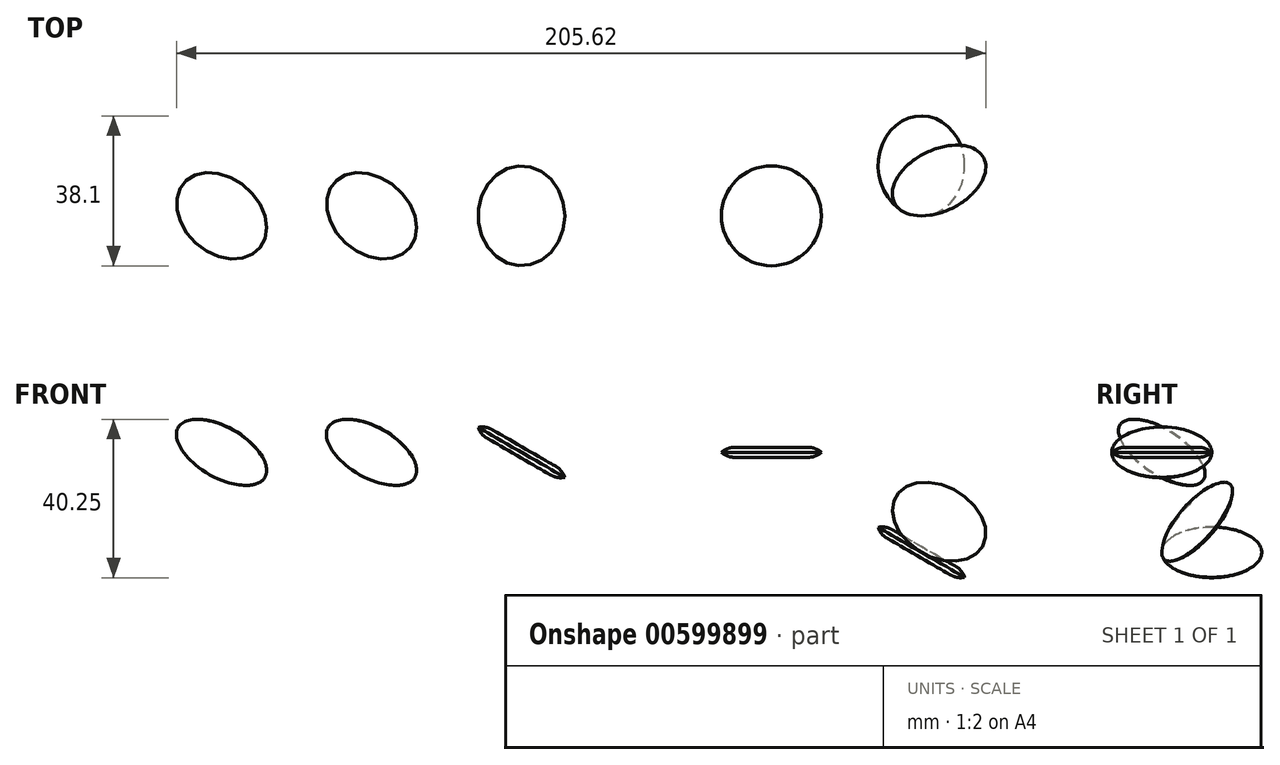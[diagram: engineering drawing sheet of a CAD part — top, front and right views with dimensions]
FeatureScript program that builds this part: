
annotation { "Feature Type Name" : "Feature", "Feature Type Description" : "" }
export const myFeature = defineFeature(function(context is Context, id is Id, definition is map)
    precondition{}
    {
        {
            var Q0;
            Q0=qCreatedBy(makeId("Top.planeOp"),FACE);
            var sketch = newSketch(context, id + "F0", { "sketchPlane" : qUnion([Q0])});
            skCircle(sketch, "E0", {"center": v(0, 0) * mm, "radius": 12.7 * mm});
            skSolve(sketch);
        }
        {
            var Q0;
            Q0 = qSketchRegion(id + "F0", true);
            extrude(context, id + "F1", {"entities" : qUnion([Q0]), "endBound" : BoundingType.SYMMETRIC, "depth" : 2.54 * mm, "offsetDistance" : 25.4 * mm});
        }
        {
            var Q0;
            Q0=makeQuery(id+"F1.opExtrude","CAP_EDGE",EDGE,{"disambiguationData":[OSD([sQuery(id+"F0.wireOp",EDGE,"E0")])],"isStart":true});
            var Q1;
            Q1=makeQuery(id+"F1.opExtrude","CAP_EDGE",EDGE,{"disambiguationData":[OSD([sQuery(id+"F0.wireOp",EDGE,"E0")])],"isStart":false});
            chamfer(context, id + "F2", {"entities" : qUnion([Q0, Q1]), "width" : 1.27 * mm, "tangentPropagation" : true});
        }
        {
            var Q0;
            {var subQ0=sQuery(id+"F0.wireOp",EDGE,"E0");Q0=makeQuery(id+"F2.opChamfer","BLEND_EDGE",EDGE,{"blendedFrom":[makeQuery(id+"F1.opExtrude","CAP_EDGE",EDGE,{"disambiguationData":[OSD([subQ0])],"isStart":false}),makeQuery(id+"F1.opExtrude","CAP_FACE",FACE,{"disambiguationData":[OSD([subQ0])],"isStart":false})],"blendedInto":[makeQuery(id+"F1.opExtrude","CAP_FACE",FACE,{"disambiguationData":[OSD([subQ0])],"isStart":false})]});}
            fillet(context, id + "F3", {"entities" : qUnion([Q0]), "radius" : 5.08 * mm, "tangentPropagation" : true, "allowEdgeOverflow" : false});
        }
        {
            var Q0;
            {var subQ0=sQuery(id+"F0.wireOp",EDGE,"E0");Q0=makeQuery(id+"F2.opChamfer","BLEND_EDGE",EDGE,{"blendedFrom":[makeQuery(id+"F1.opExtrude","CAP_EDGE",EDGE,{"disambiguationData":[OSD([subQ0])],"isStart":true}),makeQuery(id+"F1.opExtrude","CAP_FACE",FACE,{"disambiguationData":[OSD([subQ0])],"isStart":true})],"blendedInto":[makeQuery(id+"F1.opExtrude","CAP_FACE",FACE,{"disambiguationData":[OSD([subQ0])],"isStart":true})]});}
            fillet(context, id + "F4", {"entities" : qUnion([Q0]), "radius" : 5.08 * mm, "tangentPropagation" : true, "allowEdgeOverflow" : false});
        }
        {
            var Q0;
            Q0=makeQuery(id+"F1.opExtrude","SWEPT_BODY",BODY,{"disambiguationData":[OSD([sQuery(id+"F0.wireOp",EDGE,"E0")])]});
            transform(context, id + "F5", {"entities" : qUnion([Q0]), "transformType" : TransformType.TRANSLATION_3D, "dx" : 38.1 * mm, "dy" : 12.7 * mm, "dz" : -25.4 * mm, "makeCopy" : true});
        }
        {
            var Q0;
            Q0=makeQuery(id+"F5.opPattern","COPY",FACE,{"derivedFrom":makeQuery(id+"F1.opExtrude","CAP_FACE",FACE,{"disambiguationData":[OSD([sQuery(id+"F0.wireOp",EDGE,"E0")])],"isStart":false}),"instanceName":"1"});
            cPlane(context, id + "F6", {"entities" : qUnion([Q0]), "cplaneType" : CPlaneType.OFFSET, "offset" : 1.27 * mm, "oppositeDirection" : true, "width" : 152.4 * mm, "height" : 152.4 * mm});
        }
        {
            var Q0;
            Q0=qCreatedBy(id+"F6.planeOp",FACE);
            var sketch = newSketch(context, id + "F7", { "sketchPlane" : qUnion([Q0])});
            skCircle(sketch, "E1.0", {"center": v(38.1, 12.7) * mm, "radius": 9.34 * mm});
            skLineSegment(sketch, "E2", {"start": v(38.1, 12.7) * mm, "end": v(38.1, 37.81) * mm});
            skLineSegment(sketch, "E3", {"start": v(38.1, 37.81) * mm, "end": v(38.1, -2.87) * mm});
            skSolve(sketch);
        }
        {
            var Q0;
            Q0=makeQuery(id+"F5.opPattern","COPY",BODY,{"derivedFrom":makeQuery(id+"F1.opExtrude","SWEPT_BODY",BODY,{"disambiguationData":[OSD([sQuery(id+"F0.wireOp",EDGE,"E0")])]}),"instanceName":"1"});
            var Q1;
            Q1=sQuery(id+"F7.wireOp",EDGE,"E3");
            transform(context, id + "F8", {"entities" : qUnion([Q0]), "transformType" : TransformType.ROTATION, "transformAxis" : qUnion([Q1]), "angle" : 30 * degree, "oppositeDirection" : true, "makeCopy" : false});
        }
        {
            var Q0;
            Q0=makeQuery(id+"F5.opPattern","COPY",FACE,{"derivedFrom":makeQuery(id+"F1.opExtrude","CAP_FACE",FACE,{"disambiguationData":[OSD([sQuery(id+"F0.wireOp",EDGE,"E0")])],"isStart":false}),"instanceName":"1"});
            cPlane(context, id + "F9", {"entities" : qUnion([Q0]), "cplaneType" : CPlaneType.OFFSET, "offset" : 1.27 * mm, "oppositeDirection" : true, "width" : 152.4 * mm, "height" : 152.4 * mm});
        }
        {
            var Q0;
            Q0=qCreatedBy(id+"F9.planeOp",FACE);
            var sketch = newSketch(context, id + "F10", { "sketchPlane" : qUnion([Q0])});
            skCircle(sketch, "E4.0", {"center": v(45.7, 12.7) * mm, "radius": 12.7 * mm});
            skLineSegment(sketch, "E5", {"start": v(45.7, 0) * mm, "end": v(60.1, 0) * mm});
            skLineSegment(sketch, "E6", {"start": v(60.1, 0) * mm, "end": v(20.4, 0) * mm});
            skSolve(sketch);
        }
        {
            var Q0;
            Q0=makeQuery(id+"F5.opPattern","COPY",BODY,{"derivedFrom":makeQuery(id+"F1.opExtrude","SWEPT_BODY",BODY,{"disambiguationData":[OSD([sQuery(id+"F0.wireOp",EDGE,"E0")])]}),"instanceName":"1"});
            var Q1;
            Q1=sQuery(id+"F10.wireOp",EDGE,"E6");
            transform(context, id + "F11", {"entities" : qUnion([Q0]), "transformType" : TransformType.ROTATION, "transformAxis" : qUnion([Q1]), "angle" : 45 * degree, "oppositeDirection" : true, "makeCopy" : true});
        }
        {
            var Q0;
            Q0=makeQuery(id+"F1.opExtrude","SWEPT_BODY",BODY,{"disambiguationData":[OSD([sQuery(id+"F0.wireOp",EDGE,"E0")])]});
            transform(context, id + "F12", {"entities" : qUnion([Q0]), "transformType" : TransformType.TRANSLATION_3D, "dx" : -63.5 * mm, "dy" : 0 * mm, "dz" : 0 * mm, "makeCopy" : true});
        }
        {
            var Q0;
            Q0=makeQuery(id+"F12.opPattern","COPY",FACE,{"derivedFrom":makeQuery(id+"F1.opExtrude","CAP_FACE",FACE,{"disambiguationData":[OSD([sQuery(id+"F0.wireOp",EDGE,"E0")])],"isStart":false}),"instanceName":"1"});
            cPlane(context, id + "F13", {"entities" : qUnion([Q0]), "cplaneType" : CPlaneType.OFFSET, "offset" : 1.27 * mm, "oppositeDirection" : true, "width" : 152.4 * mm, "height" : 152.4 * mm});
        }
        {
            var Q0;
            Q0=qCreatedBy(id+"F13.planeOp",FACE);
            var sketch = newSketch(context, id + "F14", { "sketchPlane" : qUnion([Q0])});
            skCircle(sketch, "E7.0", {"center": v(-63.5, 0) * mm, "radius": 9.34 * mm});
            skLineSegment(sketch, "E8", {"start": v(-63.5, -21) * mm, "end": v(-63.5, 32.18) * mm});
            skSolve(sketch);
        }
        {
            var Q0;
            Q0=makeQuery(id+"F12.opPattern","COPY",BODY,{"derivedFrom":makeQuery(id+"F1.opExtrude","SWEPT_BODY",BODY,{"disambiguationData":[OSD([sQuery(id+"F0.wireOp",EDGE,"E0")])]}),"instanceName":"1"});
            var Q1;
            Q1=sQuery(id+"F14.wireOp",EDGE,"E8");
            transform(context, id + "F15", {"entities" : qUnion([Q0]), "transformType" : TransformType.ROTATION, "transformAxis" : qUnion([Q1]), "angle" : 30 * degree, "makeCopy" : false});
        }
        {
            var Q0;
            Q0=makeQuery(id+"F12.opPattern","COPY",BODY,{"derivedFrom":makeQuery(id+"F1.opExtrude","SWEPT_BODY",BODY,{"disambiguationData":[OSD([sQuery(id+"F0.wireOp",EDGE,"E0")])]}),"instanceName":"1"});
            transform(context, id + "F16", {"entities" : qUnion([Q0]), "transformType" : TransformType.TRANSLATION_3D, "dx" : -38.1 * mm, "dy" : 0 * mm, "dz" : 0 * mm, "makeCopy" : true});
        }
        {
            var Q0;
            Q0=makeQuery(id+"F16.opPattern","COPY",FACE,{"derivedFrom":makeQuery(id+"F12.opPattern","COPY",FACE,{"derivedFrom":makeQuery(id+"F1.opExtrude","CAP_FACE",FACE,{"disambiguationData":[OSD([sQuery(id+"F0.wireOp",EDGE,"E0")])],"isStart":false}),"instanceName":"1"}),"instanceName":"1"});
            cPlane(context, id + "F17", {"entities" : qUnion([Q0]), "cplaneType" : CPlaneType.OFFSET, "offset" : 1.27 * mm, "oppositeDirection" : true, "width" : 152.4 * mm, "height" : 152.4 * mm});
        }
        {
            var Q0;
            Q0=qCreatedBy(id+"F17.planeOp",FACE);
            var sketch = newSketch(context, id + "F18", { "sketchPlane" : qUnion([Q0])});
            skCircle(sketch, "E9.0", {"center": v(-87.99, 0) * mm, "radius": 9.34 * mm});
            skLineSegment(sketch, "E10", {"start": v(-115.37, 0) * mm, "end": v(-65.83, 0) * mm});
            skSolve(sketch);
        }
        {
            var Q0;
            Q0=makeQuery(id+"F16.opPattern","COPY",BODY,{"derivedFrom":makeQuery(id+"F12.opPattern","COPY",BODY,{"derivedFrom":makeQuery(id+"F1.opExtrude","SWEPT_BODY",BODY,{"disambiguationData":[OSD([sQuery(id+"F0.wireOp",EDGE,"E0")])]}),"instanceName":"1"}),"instanceName":"1"});
            var Q1;
            Q1=sQuery(id+"F18.wireOp",EDGE,"E10");
            transform(context, id + "F19", {"entities" : qUnion([Q0]), "transformType" : TransformType.ROTATION, "transformAxis" : qUnion([Q1]), "angle" : 30 * degree, "oppositeDirection" : true, "makeCopy" : false});
        }
        {
            var Q0;
            Q0=makeQuery(id+"F16.opPattern","COPY",BODY,{"derivedFrom":makeQuery(id+"F12.opPattern","COPY",BODY,{"derivedFrom":makeQuery(id+"F1.opExtrude","SWEPT_BODY",BODY,{"disambiguationData":[OSD([sQuery(id+"F0.wireOp",EDGE,"E0")])]}),"instanceName":"1"}),"instanceName":"1"});
            transform(context, id + "F20", {"entities" : qUnion([Q0]), "transformType" : TransformType.TRANSLATION_3D, "dx" : -38.1 * mm, "dy" : 0 * mm, "dz" : 0 * mm, "makeCopy" : true});
        }
    });
